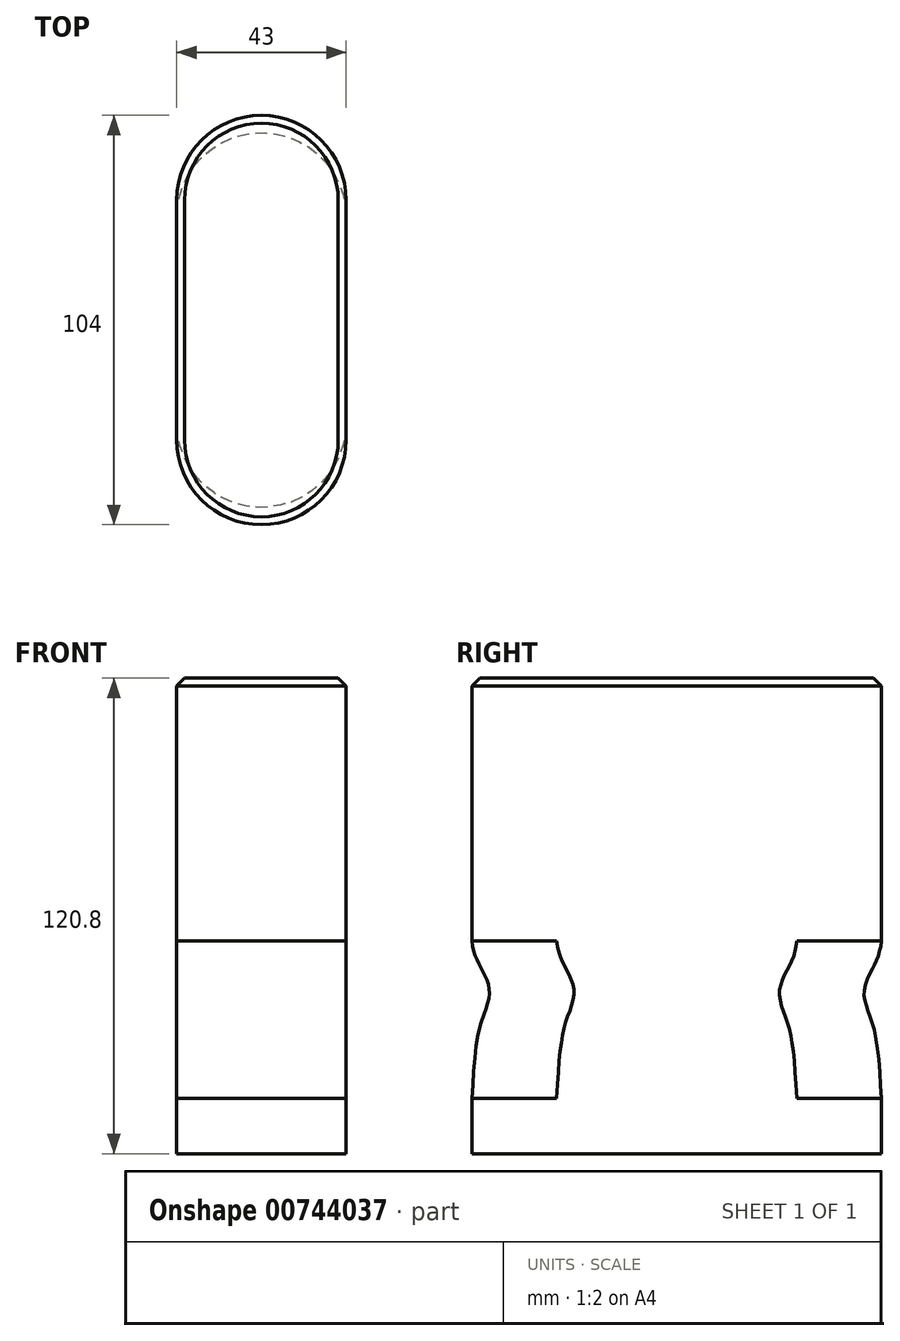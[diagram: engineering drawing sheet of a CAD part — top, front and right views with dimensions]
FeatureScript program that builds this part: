
annotation { "Feature Type Name" : "Feature", "Feature Type Description" : "" }
export const myFeature = defineFeature(function(context is Context, id is Id, definition is map)
    precondition{}
    {
        {
            var Q0;
            Q0=qCreatedBy(makeId("Top.planeOp"),FACE);
            var sketch = newSketch(context, id + "F0", { "sketchPlane" : qUnion([Q0])});
            skLineSegment(sketch, "E0.bottom", {"start": v(-21.5, 52) * mm, "end": v(21.5, 52) * mm});
            skLineSegment(sketch, "E0.top", {"start": v(-21.5, -52) * mm, "end": v(21.5, -52) * mm});
            skLineSegment(sketch, "E0.left", {"start": v(-21.5, 52) * mm, "end": v(-21.5, -52) * mm});
            skLineSegment(sketch, "E0.right", {"start": v(21.5, 52) * mm, "end": v(21.5, -52) * mm});
            skPoint(sketch, "E0.middle", {"position": v(0, 0) * mm});
            skSolve(sketch);
        }
        {
            var Q0;
            Q0=makeQuery(id+"F0.imprint","IMPRINT",FACE,{"disambiguationData":[TD([[makeQuery(id+"F0.imprint","IMPRINT",EDGE,{"derivedFrom":sQuery(id+"F0.wireOp",EDGE,"E0.bottom")}),-1.0]])]});
            extrude(context, id + "F1", {"entities" : qUnion([Q0]), "depth" : 8 * mm, "offsetDistance" : 25 * mm});
        }
        {
            var Q0;
            Q0=makeQuery(id+"F1.opExtrude","SWEPT_EDGE",EDGE,{"disambiguationData":[OSD([sQuery(id+"F0.wireOp",EDGE,"E0.top"),sQuery(id+"F0.wireOp",EDGE,"E0.left")])]});
            var Q1;
            Q1=makeQuery(id+"F1.opExtrude","SWEPT_EDGE",EDGE,{"disambiguationData":[OSD([sQuery(id+"F0.wireOp",EDGE,"E0.top"),sQuery(id+"F0.wireOp",EDGE,"E0.right")])]});
            var Q2;
            Q2=makeQuery(id+"F1.opExtrude","SWEPT_EDGE",EDGE,{"disambiguationData":[OSD([sQuery(id+"F0.wireOp",EDGE,"E0.bottom"),sQuery(id+"F0.wireOp",EDGE,"E0.right")])]});
            var Q3;
            Q3=makeQuery(id+"F1.opExtrude","SWEPT_EDGE",EDGE,{"disambiguationData":[OSD([sQuery(id+"F0.wireOp",EDGE,"E0.bottom"),sQuery(id+"F0.wireOp",EDGE,"E0.left")])]});
            fillet(context, id + "F2", {"entities" : qUnion([Q0, Q1, Q2, Q3]), "radius" : 21.5 * mm, "tangentPropagation" : true, "allowEdgeOverflow" : false});
        }
        {
            var Q0;
            Q0=makeQuery(id+"F1.opExtrude","CAP_FACE",FACE,{"disambiguationData":[OSD([sQuery(id+"F0.wireOp",EDGE,"E0.bottom"),sQuery(id+"F0.wireOp",EDGE,"E0.top"),sQuery(id+"F0.wireOp",EDGE,"E0.left"),sQuery(id+"F0.wireOp",EDGE,"E0.right")])],"isStart":false});
            var sketch = newSketch(context, id + "F3", { "sketchPlane" : qUnion([Q0])});
            skPoint(sketch, "E1", {"position": v(0, 52) * mm});
            skPoint(sketch, "E2", {"position": v(0, -52) * mm});
            skLineSegment(sketch, "E3", {"start": v(-21.5, 0) * mm, "end": v(21.5, 0) * mm});
            skSolve(sketch);
        }
        {
            var Q0;
            Q0=qCreatedBy(makeId("Right.planeOp"),FACE);
            var sketch = newSketch(context, id + "F4", { "sketchPlane" : qUnion([Q0])});
            skLineSegment(sketch, "E4", {"start": v(52, 8) * mm, "end": v(52, 14) * mm});
            skLineSegment(sketch, "E5", {"start": v(52, 54) * mm, "end": v(52, 120.8) * mm});
            skFitSpline(sketch, "E6", {"points": [v(52, 14) * mm, v(49.58, 33.52) * mm, v(47.6, 40.52) * mm, v(49.3, 46.2) * mm, v(52, 54) * mm], "startDerivative": vector(-4.75, 89.43) * mm, "endDerivative": vector(6.08, 52.1) * mm});
            skSolve(sketch);
        }
        {
            var Q0;
            Q0=qCreatedBy(makeId("Right.planeOp"),FACE);
            var sketch = newSketch(context, id + "F5", { "sketchPlane" : qUnion([Q0])});
            skLineSegment(sketch, "E7", {"start": v(-52, 8) * mm, "end": v(-52, 14) * mm});
            skLineSegment(sketch, "E8", {"start": v(-52, 54) * mm, "end": v(-52, 120.8) * mm});
            skFitSpline(sketch, "E9.MirrorCS", {"points": [v(-52, 14) * mm, v(-49.58, 33.75) * mm, v(-47.6, 40.75) * mm, v(-49.3, 46.43) * mm, v(-52, 54) * mm], "startDerivative": vector(4.75, 89.43) * mm, "endDerivative": vector(-6.08, 52.1) * mm});
            skSolve(sketch);
        }
        {
            var Q0;
            {var subQ0=sQuery(id+"F3.wireOp",EDGE,"E3");Q0=makeQuery(id+"F3.imprint","IMPRINT",FACE,{"disambiguationData":[TD([[makeQuery(id+"F3.imprint","IMPRINT",EDGE,{"derivedFrom":subQ0}),1.0]])]});}
            var Q1;
            Q1=sQuery(id+"F4.wireOp",EDGE,"E4");
            var Q2;
            Q2=sQuery(id+"F4.wireOp",EDGE,"E6");
            var Q3;
            Q3=sQuery(id+"F4.wireOp",EDGE,"E5");
            sweep(context, id + "F6", {"operationType" : NewBodyOperationType.ADD, "profiles" : qUnion([Q0]), "path" : qUnion([Q1, Q2, Q3]), "keepProfileOrientation" : true});
        }
        {
            var Q0;
            {var subQ0=sQuery(id+"F3.wireOp",EDGE,"E3");Q0=makeQuery(id+"F3.imprint","IMPRINT",FACE,{"disambiguationData":[TD([[makeQuery(id+"F3.imprint","IMPRINT",EDGE,{"derivedFrom":subQ0}),-1.0]])]});}
            var Q1;
            Q1=sQuery(id+"F5.wireOp",EDGE,"E7");
            var Q2;
            Q2=sQuery(id+"F5.wireOp",EDGE,"E9.MirrorCS");
            var Q3;
            Q3=sQuery(id+"F5.wireOp",EDGE,"E8");
            sweep(context, id + "F7", {"operationType" : NewBodyOperationType.ADD, "profiles" : qUnion([Q0]), "path" : qUnion([Q1, Q2, Q3]), "keepProfileOrientation" : true});
        }
        {
            var Q0;
            {var subQ0=sQuery(id+"F3.wireOp",EDGE,"E3");var subQ1=sQuery(id+"F0.wireOp",EDGE,"E0.right");var subQ2=sQuery(id+"F0.wireOp",EDGE,"E0.left");var subQ3=sQuery(id+"F0.wireOp",EDGE,"E0.top");var subQ4=sQuery(id+"F0.wireOp",EDGE,"E0.bottom");Q0=makeQuery(id+"F7.boolean.opBoolean","MERGE",FACE,{"derivedFrom":[makeQuery(id+"F6.opSweep","CAP_FACE",FACE,{"disambiguationData":[OSD([subQ4,subQ3,subQ2,subQ1,subQ0,sQuery(id+"F4.wireOp",VERTEX,"E5.end")])],"isStart":false}),makeQuery(id+"F7.opSweep","CAP_FACE",FACE,{"disambiguationData":[OSD([subQ4,subQ3,subQ2,subQ1,subQ0,sQuery(id+"F5.wireOp",VERTEX,"E8.end")])],"isStart":false})]});}
            chamfer(context, id + "F8", {"entities" : qUnion([Q0]), "width" : 2 * mm, "tangentPropagation" : true});
        }
    });
